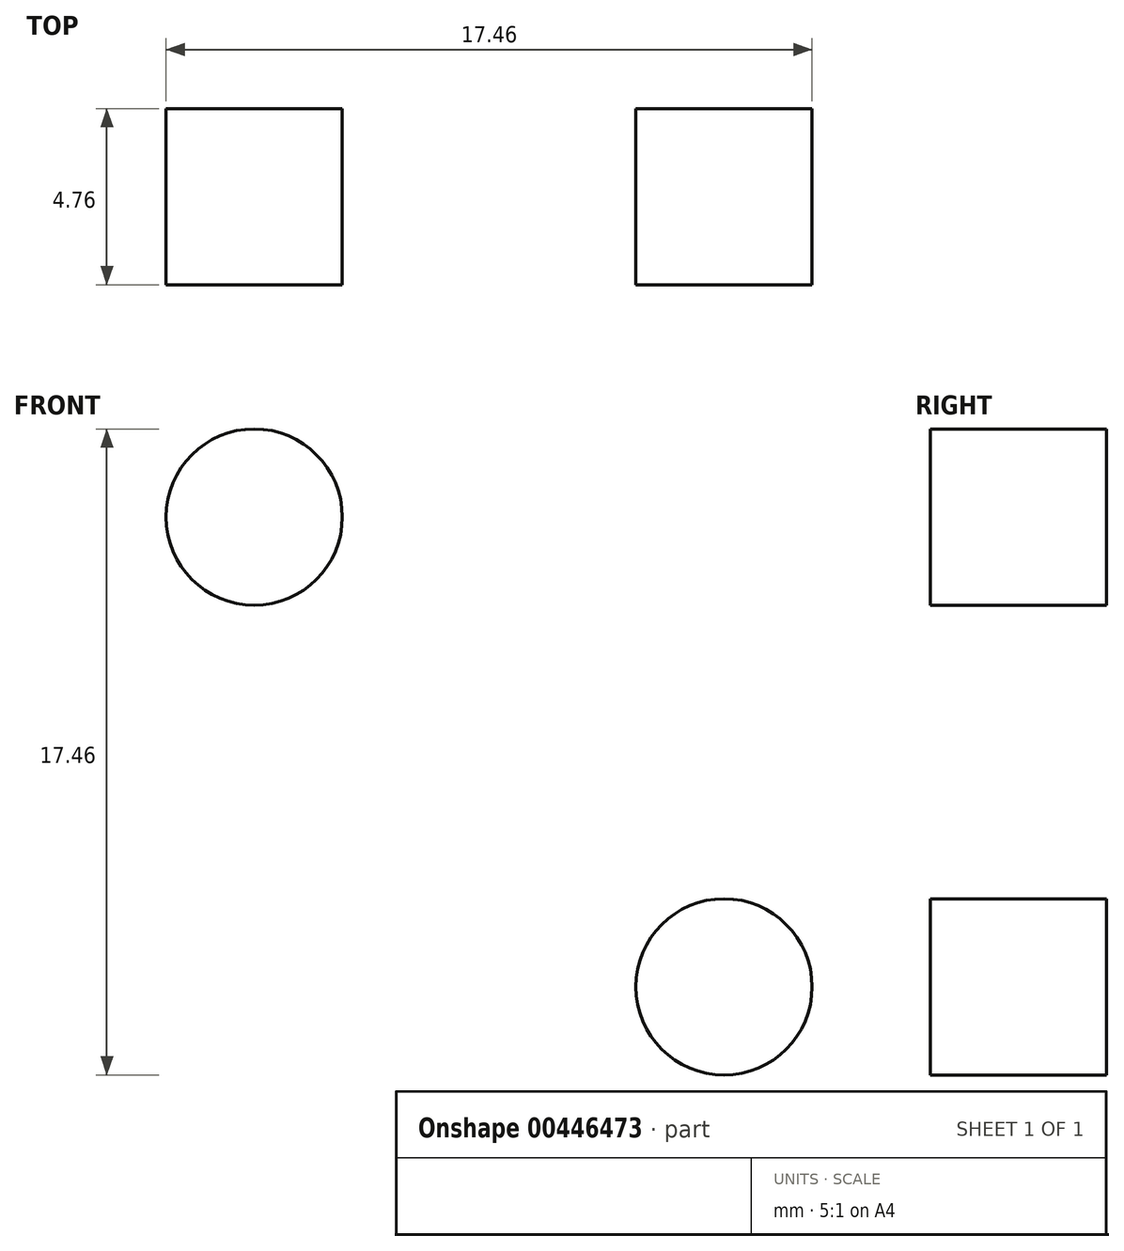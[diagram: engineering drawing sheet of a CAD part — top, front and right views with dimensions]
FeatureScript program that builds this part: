
annotation { "Feature Type Name" : "Feature", "Feature Type Description" : "" }
export const myFeature = defineFeature(function(context is Context, id is Id, definition is map)
    precondition{}
    {
        {
            var Q0;
            Q0=qCreatedBy(makeId("Right.planeOp"),FACE);
            var sketch = newSketch(context, id + "F0", { "sketchPlane" : qUnion([Q0])});
            skLineSegment(sketch, "E0", {"start": v(0, 76.2) * mm, "end": v(0, 0) * mm});
            skLineSegment(sketch, "E1", {"start": v(0, 0) * mm, "end": v(76.2, 0) * mm});
            skLineSegment(sketch, "E2", {"start": v(0, 76.2) * mm, "end": v(0, 76.2) * mm});
            skLineSegment(sketch, "E3", {"start": v(4.76, 71.44) * mm, "end": v(4.76, 12.7) * mm});
            skLineSegment(sketch, "E4", {"start": v(12.7, 4.76) * mm, "end": v(71.44, 4.76) * mm});
            skLineSegment(sketch, "E5", {"start": v(76.2, 0) * mm, "end": v(76.2, 0) * mm});
            skPoint(sketch, "E6.visualSharp", {"position": v(4.76, 4.76) * mm});
            skArc(sketch, "E6.filletArc", {"start": v(4.76, 12.7) * mm, "mid": v(7.09, 7.09) * mm, "end": v(12.7, 4.76) * mm});
            skPoint(sketch, "E7.visualSharp", {"position": v(4.76, 76.2) * mm});
            skArc(sketch, "E7.filletArc", {"start": v(4.76, 71.44) * mm, "mid": v(3.37, 74.8) * mm, "end": v(0, 76.2) * mm});
            skPoint(sketch, "E8.visualSharp", {"position": v(76.2, 4.76) * mm});
            skArc(sketch, "E8.filletArc", {"start": v(76.2, 0) * mm, "mid": v(74.8, 3.37) * mm, "end": v(71.44, 4.76) * mm});
            skSolve(sketch);
        }
        {
            var Q0;
            Q0=makeQuery(id+"F0.imprint","IMPRINT",FACE,{"disambiguationData":[TD([[makeQuery(id+"F0.imprint","IMPRINT",EDGE,{"derivedFrom":sQuery(id+"F0.wireOp",EDGE,"E0")}),1.0]])]});
            extrude(context, id + "F1", {"entities" : qUnion([Q0]), "depth" : 368.3 * mm, "offsetDistance" : 25.4 * mm, "symmetric" : true});
        }
        {
            var Q0;
            Q0=makeQuery(id+"F1.opExtrude","SWEPT_FACE",FACE,{"disambiguationData":[OSD([sQuery(id+"F0.wireOp",EDGE,"E3")])]});
            var sketch = newSketch(context, id + "F2", { "sketchPlane" : qUnion([Q0])});
            skLineSegment(sketch, "E9.bottom", {"start": v(158.75, 139.7) * mm, "end": v(-158.75, 139.7) * mm});
            skLineSegment(sketch, "E9.top", {"start": v(158.75, 12.7) * mm, "end": v(-158.75, 12.7) * mm});
            skLineSegment(sketch, "E9.left", {"start": v(158.75, 139.7) * mm, "end": v(158.75, 12.7) * mm});
            skLineSegment(sketch, "E9.right", {"start": v(-158.75, 139.7) * mm, "end": v(-158.75, 12.7) * mm});
            skPoint(sketch, "E9.middle", {"position": v(0, 76.2) * mm});
            skSolve(sketch);
        }
        {
            var Q0;
            {var subQ0=sQuery(id+"F2.wireOp",EDGE,"E9.bottom");Q0=makeQuery(id+"F2.imprint","IMPRINT",FACE,{"disambiguationData":[TD([[makeQuery(id+"F2.imprint","IMPRINT",EDGE,{"derivedFrom":subQ0}),1.0]])]});}
            var Q1;
            {var subQ0=sQuery(id+"F2.wireOp",EDGE,"E9.top");Q1=makeQuery(id+"F2.imprint","IMPRINT",FACE,{"disambiguationData":[TD([[makeQuery(id+"F2.imprint","IMPRINT",EDGE,{"derivedFrom":subQ0}),1.0]])]});}
            extrude(context, id + "F3", {"entities" : qUnion([Q0, Q1]), "operationType" : NewBodyOperationType.REMOVE, "endBound" : BoundingType.THROUGH_ALL, "oppositeDirection" : true, "depth" : 25.4 * mm, "offsetDistance" : 25.4 * mm});
        }
        {
            var Q0;
            Q0=makeQuery(id+"F3.boolean.opBoolean","COPY",EDGE,{"derivedFrom":makeQuery(id+"F3.opExtrude","SWEPT_EDGE",EDGE,{"disambiguationData":[OSD([sQuery(id+"F0.wireOp",EDGE,"5OPbmFIV-ildq-i1dt-bXUS-jtd5jzJriUmc"),sQuery(id+"F0.wireOp",EDGE,"a9fffc1a-9b01-4b6f-95ef-033cc12c7e61.filletArc"),sQuery(id+"F2.wireOp",EDGE,"E9.top"),sQuery(id+"F2.wireOp",EDGE,"E9.right")])]})});
            var Q1;
            Q1=makeQuery(id+"F3.boolean.opBoolean","COPY",EDGE,{"derivedFrom":makeQuery(id+"F3.opExtrude","SWEPT_EDGE",EDGE,{"disambiguationData":[OSD([sQuery(id+"F0.wireOp",EDGE,"5OPbmFIV-ildq-i1dt-bXUS-jtd5jzJriUmc"),sQuery(id+"F0.wireOp",EDGE,"a9fffc1a-9b01-4b6f-95ef-033cc12c7e61.filletArc"),sQuery(id+"F2.wireOp",EDGE,"E9.top"),sQuery(id+"F2.wireOp",EDGE,"E9.left")])]})});
            fillet(context, id + "F4", {"entities" : qUnion([Q0, Q1]), "radius" : 5.08 * mm, "tangentPropagation" : true, "allowEdgeOverflow" : false});
        }
        {
            var Q0;
            Q0=makeQuery(id+"F1.opExtrude","SWEPT_FACE",FACE,{"disambiguationData":[OSD([sQuery(id+"F0.wireOp",EDGE,"E0")])]});
            var sketch = newSketch(context, id + "F5", { "sketchPlane" : qUnion([Q0])});
            skPoint(sketch, "E10", {"position": v(177.8, 63.5) * mm});
            skPoint(sketch, "E11", {"position": v(165.1, 50.8) * mm});
            skLineSegment(sketch, "E12", {"start": v(0, 0) * mm, "end": v(0, 116.75) * mm, "construction": true});
            skCircle(sketch, "E13", {"center": v(165.1, 50.8) * mm, "radius": 2.38 * mm});
            skCircle(sketch, "E14", {"center": v(177.8, 63.5) * mm, "radius": 2.38 * mm});
            skCircle(sketch, "E15.MirrorC", {"center": v(-165.1, 50.8) * mm, "radius": 2.38 * mm});
            skCircle(sketch, "E16.MirrorC", {"center": v(-177.8, 63.5) * mm, "radius": 2.38 * mm});
            skSolve(sketch);
        }
        {
            var Q0;
            Q0=makeQuery(id+"F5.imprint","IMPRINT",FACE,{"disambiguationData":[TD([[makeQuery(id+"F5.imprint","IMPRINT",EDGE,{"derivedFrom":sQuery(id+"F5.wireOp",EDGE,"E15.MirrorC")}),-1.0]])]});
            var Q1;
            Q1=makeQuery(id+"F5.imprint","IMPRINT",FACE,{"disambiguationData":[TD([[makeQuery(id+"F5.imprint","IMPRINT",EDGE,{"derivedFrom":sQuery(id+"F5.wireOp",EDGE,"E16.MirrorC")}),-1.0]])]});
            var Q2;
            Q2=makeQuery(id+"F5.imprint","IMPRINT",FACE,{"disambiguationData":[TD([[makeQuery(id+"F5.imprint","IMPRINT",EDGE,{"derivedFrom":sQuery(id+"F5.wireOp",EDGE,"E14")}),1.0]])]});
            var Q3;
            Q3=makeQuery(id+"F5.imprint","IMPRINT",FACE,{"disambiguationData":[TD([[makeQuery(id+"F5.imprint","IMPRINT",EDGE,{"derivedFrom":sQuery(id+"F5.wireOp",EDGE,"E13")}),1.0]])]});
            extrude(context, id + "F6", {"entities" : qUnion([Q0, Q1, Q2, Q3]), "operationType" : NewBodyOperationType.REMOVE, "endBound" : BoundingType.THROUGH_ALL, "oppositeDirection" : true, "depth" : 25.4 * mm, "offsetDistance" : 25.4 * mm});
        }
    });
